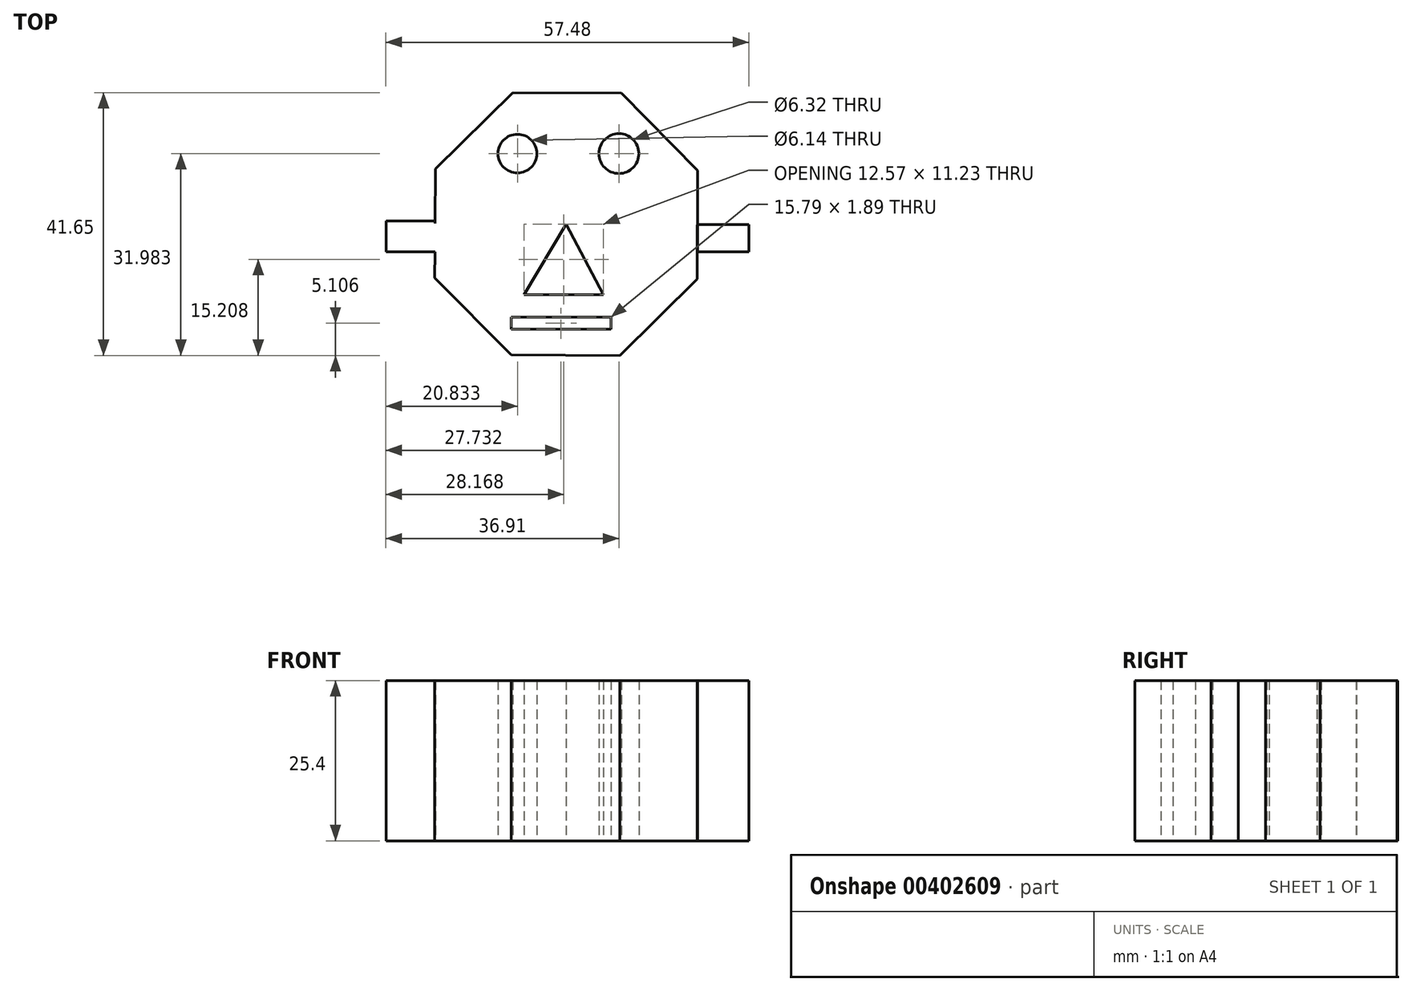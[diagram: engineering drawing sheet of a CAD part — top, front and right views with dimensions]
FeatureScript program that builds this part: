
annotation { "Feature Type Name" : "Feature", "Feature Type Description" : "" }
export const myFeature = defineFeature(function(context is Context, id is Id, definition is map)
    precondition{}
    {
        {
            var Q0;
            Q0=qCreatedBy(makeId("Top.planeOp"),FACE);
            var sketch = newSketch(context, id + "F0", { "sketchPlane" : qUnion([Q0])});
            skCircle(sketch, "E0.cCircle", {"center": v(-8.34, 4.43) * mm, "radius": 22.5 * mm, "construction": true});
            skLineSegment(sketch, "E0.0", {"start": v(12.49, 12.93) * mm, "end": v(12.4, -4.28) * mm});
            skLineSegment(sketch, "E0.1", {"start": v(12.4, -4.28) * mm, "end": v(0.16, -16.4) * mm});
            skLineSegment(sketch, "E0.2", {"start": v(0.16, -16.4) * mm, "end": v(-17.05, -16.3) * mm});
            skLineSegment(sketch, "E0.3", {"start": v(-17.05, -16.3) * mm, "end": v(-29.16, -4.07) * mm});
            skLineSegment(sketch, "E0.4", {"start": v(-29.16, -4.07) * mm, "end": v(-29.14, 0) * mm});
            skLineSegment(sketch, "E0.5", {"start": v(-29.07, 13.15) * mm, "end": v(-16.84, 25.26) * mm});
            skLineSegment(sketch, "E0.6", {"start": v(-16.84, 25.26) * mm, "end": v(0.38, 25.17) * mm});
            skLineSegment(sketch, "E0.7", {"start": v(0.38, 25.17) * mm, "end": v(12.49, 12.93) * mm});
            skLineSegment(sketch, "E1.top", {"start": v(-15.03, -6.8) * mm, "end": v(-2.46, -6.8) * mm});
            skPoint(sketch, "E2.firstSnap0", {"position": v(-29.12, 4.54) * mm});
            skLineSegment(sketch, "E2.left", {"start": v(-30.83, 4.54) * mm, "end": v(-30.83, 4.32) * mm});
            skLineSegment(sketch, "E3.left", {"start": v(12.44, 4.32) * mm, "end": v(12.44, 0) * mm});
            skPoint(sketch, "E4", {"position": v(-16.08, 15.6) * mm});
            skPoint(sketch, "E5", {"position": v(0, 15.6) * mm});
            skCircle(sketch, "E6", {"center": v(-16.08, 15.6) * mm, "radius": 3.07 * mm});
            skLineSegment(sketch, "E7", {"start": v(-15.03, -6.8) * mm, "end": v(-8.34, 4.43) * mm});
            skLineSegment(sketch, "E8", {"start": v(-8.34, 4.43) * mm, "end": v(-2.46, -6.8) * mm});
            skCircle(sketch, "E9", {"center": v(0, 15.6) * mm, "radius": 3.16 * mm});
            skPoint(sketch, "E10.end.orphan", {"position": v(20.57, -19.14) * mm});
            skPoint(sketch, "E10.start.orphan", {"position": v(20.57, -23.53) * mm});
            skPoint(sketch, "E11.orphan", {"position": v(-30.83, 0) * mm});
            skPoint(sketch, "E12.end.orphan", {"position": v(-36.9, 0) * mm});
            skLineSegment(sketch, "E13", {"start": v(-30.39, 0) * mm, "end": v(-30.83, 0) * mm});
            skLineSegment(sketch, "E14", {"start": v(-29.12, 4.54) * mm, "end": v(-29.14, 0) * mm});
            skLineSegment(sketch, "E15", {"start": v(-30.83, 0) * mm, "end": v(-30.39, 0) * mm});
            skPoint(sketch, "E16.firstSnap0", {"position": v(6.28, -10.34) * mm});
            skLineSegment(sketch, "E16.bottom", {"start": v(-1.28, -10.34) * mm, "end": v(-17.07, -10.34) * mm});
            skLineSegment(sketch, "E16.top", {"start": v(-1.28, -12.23) * mm, "end": v(-17.07, -12.23) * mm});
            skLineSegment(sketch, "E16.left", {"start": v(-1.28, -10.34) * mm, "end": v(-1.28, -12.23) * mm});
            skLineSegment(sketch, "E16.right", {"start": v(-17.07, -10.34) * mm, "end": v(-17.07, -12.23) * mm});
            skPoint(sketch, "E17.orphan", {"position": v(-36.9, 4.94) * mm});
            skPoint(sketch, "E18.end.orphan", {"position": v(-29.12, 4.9) * mm});
            skLineSegment(sketch, "E19.trimOffspring", {"start": v(-29.12, 4.54) * mm, "end": v(-29.07, 13.15) * mm});
            skPoint(sketch, "E3.right.end.orphan", {"position": v(20.57, 0) * mm});
            skLineSegment(sketch, "E20.bottom", {"start": v(12.44, 4.32) * mm, "end": v(20.57, 4.32) * mm});
            skLineSegment(sketch, "E20.top", {"start": v(12.44, 0) * mm, "end": v(20.57, 0) * mm});
            skLineSegment(sketch, "E20.right", {"start": v(20.57, 4.32) * mm, "end": v(20.57, 0) * mm});
            skLineSegment(sketch, "E21.bottom", {"start": v(-29.12, 4.9) * mm, "end": v(-36.9, 4.9) * mm});
            skLineSegment(sketch, "E21.top", {"start": v(-29.12, 0) * mm, "end": v(-36.9, 0) * mm});
            skLineSegment(sketch, "E21.left", {"start": v(-29.12, 4.9) * mm, "end": v(-29.12, 0) * mm});
            skLineSegment(sketch, "E21.right", {"start": v(-36.9, 4.9) * mm, "end": v(-36.9, 0) * mm});
            skSolve(sketch);
        }
        {
            var Q0;
            Q0 = qSketchRegion(id + "F0", true);
            extrude(context, id + "F1", {"entities" : qUnion([Q0]), "depth" : 25.4 * mm});
        }
    });
